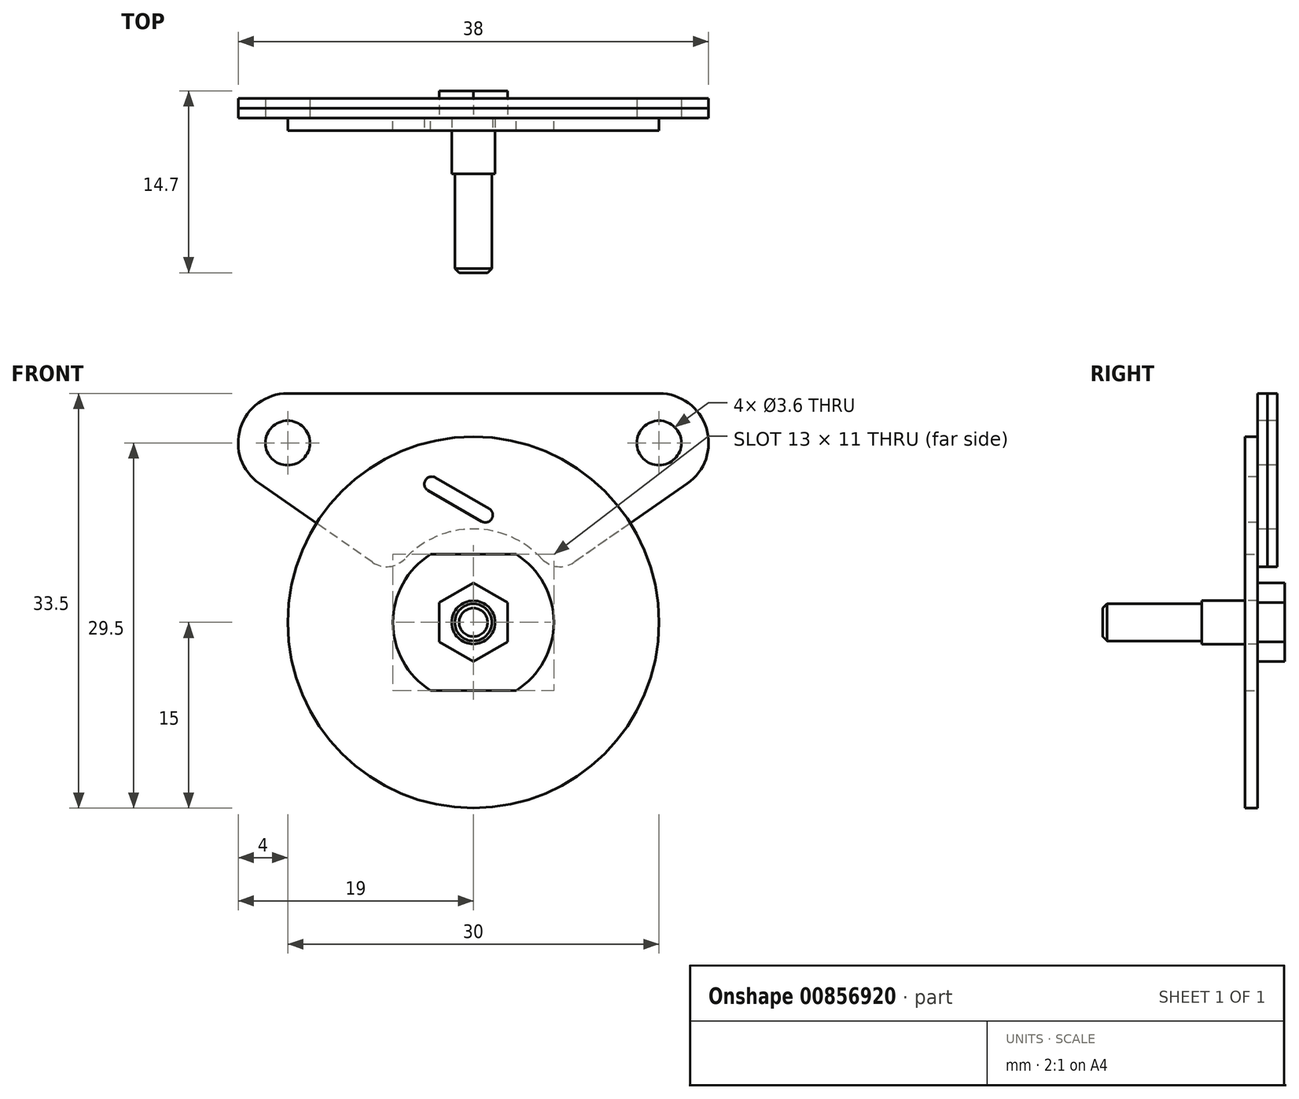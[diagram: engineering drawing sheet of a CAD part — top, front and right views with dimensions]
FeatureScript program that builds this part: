
annotation { "Feature Type Name" : "Feature", "Feature Type Description" : "" }
export const myFeature = defineFeature(function(context is Context, id is Id, definition is map)
    precondition{}
    {
        {
            var Q0;
            Q0=qCreatedBy(makeId("Front.planeOp"),FACE);
            var sketch = newSketch(context, id + "F0", { "sketchPlane" : qUnion([Q0])});
            skCircle(sketch, "E0", {"center": v(0, 0) * mm, "radius": 15 * mm});
            skArc(sketch, "E1", {"start": v(-3.46, 5.5) * mm, "mid": v(-6.5, 0) * mm, "end": v(-3.46, -5.5) * mm});
            skLineSegment(sketch, "E2", {"start": v(0, 0) * mm, "end": v(-24.22, 0) * mm, "construction": true});
            skLineSegment(sketch, "E3", {"start": v(-3.46, 5.5) * mm, "end": v(3.46, 5.5) * mm});
            skLineSegment(sketch, "E4", {"start": v(3.46, -5.5) * mm, "end": v(-3.46, -5.5) * mm});
            skArc(sketch, "E5.trimOffspring", {"start": v(3.46, -5.5) * mm, "mid": v(6.5, 0) * mm, "end": v(3.46, 5.5) * mm});
            skSolve(sketch);
        }
        {
            var Q0;
            Q0 = qSketchRegion(id + "F0", true);
            extrude(context, id + "F1", {"entities" : qUnion([Q0]), "depth" : 1 * mm, "offsetDistance" : 25 * mm});
        }
        {
            var Q0;
            Q0=makeQuery(id+"F1.opExtrude","CAP_FACE",FACE,{"disambiguationData":[OSD([sQuery(id+"F0.wireOp",EDGE,"E0"),sQuery(id+"F0.wireOp",EDGE,"E1"),sQuery(id+"F0.wireOp",EDGE,"E3"),sQuery(id+"F0.wireOp",EDGE,"E4"),sQuery(id+"F0.wireOp",EDGE,"E5.trimOffspring")])],"isStart":false});
            var sketch = newSketch(context, id + "F2", { "sketchPlane" : qUnion([Q0])});
            skLineSegment(sketch, "E6", {"start": v(-3.36, 11.18) * mm, "end": v(0.97, 8.68) * mm, "construction": true});
            skArc(sketch, "E7.0.startCap", {"start": v(-3.66, 10.66) * mm, "mid": v(-3.88, 11.48) * mm, "end": v(-3.06, 11.7) * mm});
            skArc(sketch, "E7.0.endCap", {"start": v(1.27, 9.2) * mm, "mid": v(1.49, 8.38) * mm, "end": v(0.67, 8.16) * mm});
            skLineSegment(sketch, "E7.0.left", {"start": v(-3.06, 11.7) * mm, "end": v(1.27, 9.2) * mm});
            skLineSegment(sketch, "E7.0.right", {"start": v(-3.66, 10.66) * mm, "end": v(0.67, 8.16) * mm});
            skLineSegment(sketch, "E8", {"start": v(-1.2, 9.93) * mm, "end": v(-2.05, 8.46) * mm, "construction": true});
            skSolve(sketch);
        }
        {
            var Q0;
            Q0 = qSketchRegion(id + "F2", true);
            extrude(context, id + "F3", {"entities" : qUnion([Q0]), "operationType" : NewBodyOperationType.REMOVE, "oppositeDirection" : true, "depth" : 25 * mm, "offsetDistance" : 25 * mm});
        }
        {
            var Q0;
            Q0=qCreatedBy(makeId("Front.planeOp"),FACE);
            var sketch = newSketch(context, id + "F4", { "sketchPlane" : qUnion([Q0])});
            skLineSegment(sketch, "E9", {"start": v(15, 14.5) * mm, "end": v(-15, 14.5) * mm, "construction": true});
            skLineSegment(sketch, "E10", {"start": v(7, 6.5) * mm, "end": v(-7, 6.5) * mm, "construction": true});
            skArc(sketch, "E11", {"start": v(17.28, 11.22) * mm, "mid": v(18.82, 15.7) * mm, "end": v(15, 18.5) * mm});
            skArc(sketch, "E12", {"start": v(-15, 18.5) * mm, "mid": v(-18.82, 15.7) * mm, "end": v(-17.28, 11.22) * mm});
            skArc(sketch, "E13", {"start": v(-8.14, 4.86) * mm, "mid": v(-6.79, 4.51) * mm, "end": v(-5.53, 5.14) * mm});
            skArc(sketch, "E14", {"start": v(5.53, 5.14) * mm, "mid": v(6.79, 4.51) * mm, "end": v(8.14, 4.86) * mm});
            skCircle(sketch, "E15", {"center": v(15, 14.5) * mm, "radius": 1.8 * mm});
            skCircle(sketch, "E16", {"center": v(-15, 14.5) * mm, "radius": 1.8 * mm});
            skLineSegment(sketch, "E17", {"start": v(15, 14.5) * mm, "end": v(15, 18.5) * mm, "construction": true});
            skLineSegment(sketch, "E18", {"start": v(15, 18.5) * mm, "end": v(-15, 18.5) * mm});
            skLineSegment(sketch, "E19", {"start": v(-15, 18.5) * mm, "end": v(-15, 14.5) * mm, "construction": true});
            skArc(sketch, "E20", {"start": v(5.53, 5.14) * mm, "mid": v(0, 7.55) * mm, "end": v(-5.53, 5.14) * mm});
            skLineSegment(sketch, "E21", {"start": v(0, 14.5) * mm, "end": v(0, 6.5) * mm, "construction": true});
            skLineSegment(sketch, "E22", {"start": v(17.28, 11.22) * mm, "end": v(8.14, 4.86) * mm});
            skLineSegment(sketch, "E23", {"start": v(-8.14, 4.86) * mm, "end": v(-17.28, 11.22) * mm});
            skSolve(sketch);
        }
        {
            var Q0;
            Q0 = qSketchRegion(id + "F4", true);
            extrude(context, id + "F5", {"entities" : qUnion([Q0]), "oppositeDirection" : true, "depth" : 0.8 * mm, "offsetDistance" : 25 * mm});
        }
        {
            var Q0;
            Q0=makeQuery(id+"F5.opExtrude","SWEPT_BODY",BODY,{"disambiguationData":[OSD([sQuery(id+"F4.wireOp",EDGE,"E11"),sQuery(id+"F4.wireOp",EDGE,"E12"),sQuery(id+"F4.wireOp",EDGE,"E13"),sQuery(id+"F4.wireOp",EDGE,"E14"),sQuery(id+"F4.wireOp",EDGE,"E15"),sQuery(id+"F4.wireOp",EDGE,"E16"),sQuery(id+"F4.wireOp",EDGE,"E18"),sQuery(id+"F4.wireOp",EDGE,"E20"),sQuery(id+"F4.wireOp",EDGE,"E22"),sQuery(id+"F4.wireOp",EDGE,"E23")])]});
            transform(context, id + "F6", {"entities" : qUnion([Q0]), "transformType" : TransformType.TRANSLATION_3D, "dx" : 0 * mm, "dy" : 0.8 * mm, "dz" : 0 * mm, "makeCopy" : true});
        }
        {
            var Q0;
            Q0=qCreatedBy(makeId("Top.planeOp"),FACE);
            var sketch = newSketch(context, id + "F7", { "sketchPlane" : qUnion([Q0])});
            skLineSegment(sketch, "E24", {"start": v(0, 0) * mm, "end": v(0, -12.5) * mm});
            skLineSegment(sketch, "E25", {"start": v(0, -12.5) * mm, "end": v(-1.5, -12.5) * mm});
            skLineSegment(sketch, "E26", {"start": v(-1.5, -12.5) * mm, "end": v(-1.5, -4.5) * mm});
            skLineSegment(sketch, "E27", {"start": v(-1.5, -4.5) * mm, "end": v(-1.75, -4.5) * mm});
            skLineSegment(sketch, "E28", {"start": v(-1.75, -4.5) * mm, "end": v(-1.75, 0) * mm});
            skLineSegment(sketch, "E29", {"start": v(-1.75, 0) * mm, "end": v(0, 0) * mm});
            skLineSegment(sketch, "E30", {"start": v(0, 0) * mm, "end": v(0, 0.89) * mm, "construction": true});
            skSolve(sketch);
        }
        {
            var Q0;
            Q0 = qSketchRegion(id + "F7", true);
            var Q1;
            Q1=sQuery(id+"F7.wireOp",EDGE,"E30");
            revolve(context, id + "F8", {"surfaceOperationType" : NewSurfaceOperationType.NEW, "entities" : qUnion([Q0]), "axis" : qUnion([Q1]), "revolveType" : RevolveType.FULL});
        }
        {
            var Q0;
            Q0=makeQuery(id+"F8.opRevolve","SWEPT_FACE",FACE,{"disambiguationData":[OSD([sQuery(id+"F7.wireOp",EDGE,"E29")])]});
            var sketch = newSketch(context, id + "F9", { "sketchPlane" : qUnion([Q0])});
            skCircle(sketch, "E31.cCircle", {"center": v(0, 0) * mm, "radius": 2.75 * mm, "construction": true});
            skLineSegment(sketch, "E31.0", {"start": v(2.75, 1.59) * mm, "end": v(2.75, -1.59) * mm});
            skLineSegment(sketch, "E31.1", {"start": v(2.75, -1.59) * mm, "end": v(0, -3.18) * mm});
            skLineSegment(sketch, "E31.2", {"start": v(0, -3.18) * mm, "end": v(-2.75, -1.59) * mm});
            skLineSegment(sketch, "E31.3", {"start": v(-2.75, -1.59) * mm, "end": v(-2.75, 1.59) * mm});
            skLineSegment(sketch, "E31.4", {"start": v(-2.75, 1.59) * mm, "end": v(0, 3.18) * mm});
            skLineSegment(sketch, "E31.5", {"start": v(0, 3.18) * mm, "end": v(2.75, 1.59) * mm});
            skPoint(sketch, "E31.0.midPoint", {"position": v(2.75, 0) * mm});
            skSolve(sketch);
        }
        {
            var Q0;
            Q0 = qSketchRegion(id + "F9", true);
            extrude(context, id + "F10", {"entities" : qUnion([Q0]), "operationType" : NewBodyOperationType.ADD, "depth" : 2.2 * mm, "offsetDistance" : 25 * mm});
        }
        {
            var Q0;
            Q0=makeQuery(id+"F8.opRevolve","SWEPT_EDGE",EDGE,{"disambiguationData":[OSD([sQuery(id+"F7.wireOp",EDGE,"E25"),sQuery(id+"F7.wireOp",EDGE,"E26")])]});
            chamfer(context, id + "F11", {"entities" : qUnion([Q0]), "width" : 0.35 * mm, "tangentPropagation" : true});
        }
    });
